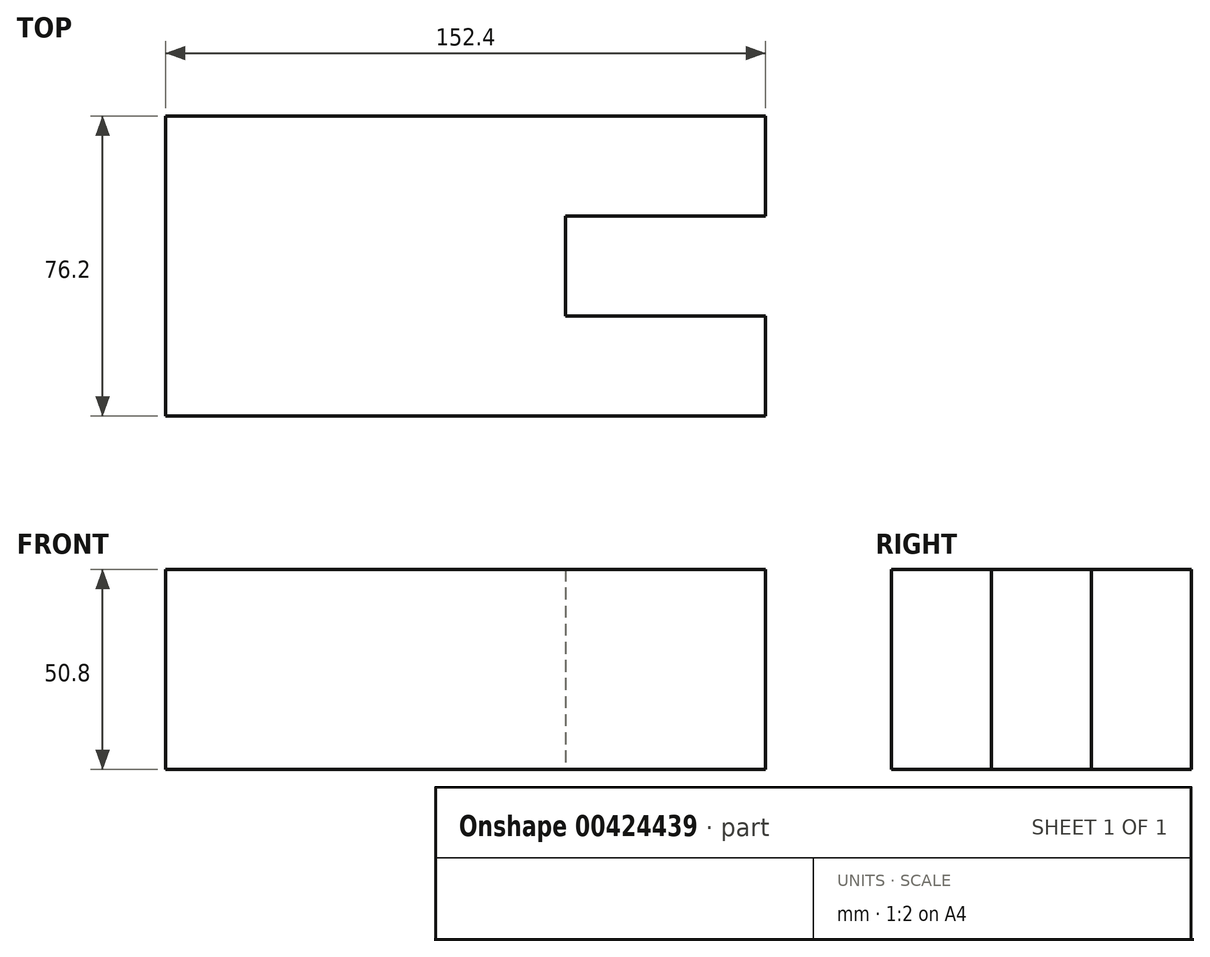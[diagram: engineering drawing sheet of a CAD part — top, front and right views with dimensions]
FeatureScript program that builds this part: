
annotation { "Feature Type Name" : "Feature", "Feature Type Description" : "" }
export const myFeature = defineFeature(function(context is Context, id is Id, definition is map)
    precondition{}
    {
        {
            var Q0;
            Q0=qCreatedBy(makeId("Top.planeOp"),FACE);
            var sketch = newSketch(context, id + "F0", { "sketchPlane" : qUnion([Q0])});
            skLineSegment(sketch, "E0", {"start": v(0, 0) * mm, "end": v(152.4, 0) * mm});
            skLineSegment(sketch, "E1", {"start": v(152.4, 0) * mm, "end": v(152.4, -25.4) * mm});
            skLineSegment(sketch, "E2", {"start": v(152.4, -25.4) * mm, "end": v(101.6, -25.4) * mm});
            skLineSegment(sketch, "E3", {"start": v(101.6, -25.4) * mm, "end": v(101.6, -50.8) * mm});
            skLineSegment(sketch, "E4", {"start": v(101.6, -50.8) * mm, "end": v(152.4, -50.8) * mm});
            skLineSegment(sketch, "E5", {"start": v(152.4, -50.8) * mm, "end": v(152.4, -76.2) * mm});
            skLineSegment(sketch, "E6", {"start": v(152.4, -76.2) * mm, "end": v(0, -76.2) * mm});
            skLineSegment(sketch, "E7", {"start": v(0, -76.2) * mm, "end": v(0, 0) * mm});
            skSolve(sketch);
        }
        {
            var Q0;
            Q0=makeQuery(id+"F0.imprint","IMPRINT",FACE,{"disambiguationData":[TD([[makeQuery(id+"F0.imprint","IMPRINT",EDGE,{"derivedFrom":sQuery(id+"F0.wireOp",EDGE,"E0")}),-1.0]])]});
            extrude(context, id + "F1", {"entities" : qUnion([Q0]), "depth" : 50.8 * mm});
        }
    });
